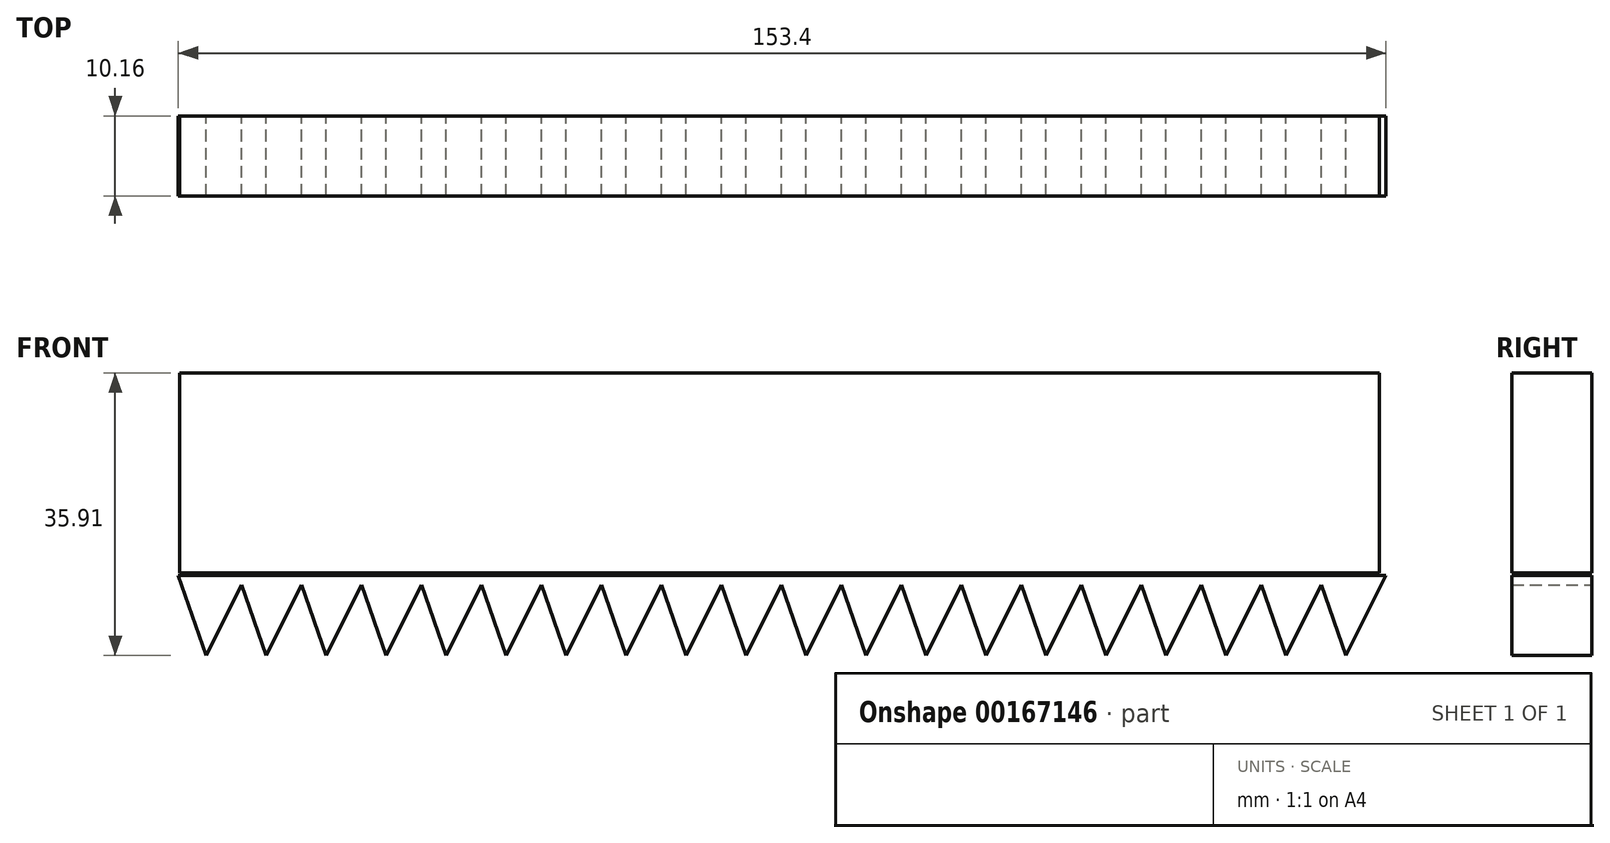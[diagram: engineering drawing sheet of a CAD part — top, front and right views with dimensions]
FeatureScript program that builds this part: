
annotation { "Feature Type Name" : "Feature", "Feature Type Description" : "" }
export const myFeature = defineFeature(function(context is Context, id is Id, definition is map)
    precondition{}
    {
        {
            var Q0;
            Q0=qCreatedBy(makeId("Front.planeOp"),FACE);
            var sketch = newSketch(context, id + "F0", { "sketchPlane" : qUnion([Q0])});
            skLineSegment(sketch, "E0.bottom", {"start": v(-76.2, 12.7) * mm, "end": v(76.2, 12.7) * mm});
            skLineSegment(sketch, "E0.top", {"start": v(-76.2, -12.7) * mm, "end": v(76.2, -12.7) * mm});
            skLineSegment(sketch, "E0.left", {"start": v(-76.2, 12.7) * mm, "end": v(-76.2, -12.7) * mm});
            skLineSegment(sketch, "E0.right", {"start": v(76.2, 12.7) * mm, "end": v(76.2, -12.7) * mm});
            skPoint(sketch, "E0.middle", {"position": v(0, 0) * mm});
            skSolve(sketch);
        }
        {
            var Q0;
            Q0=qCreatedBy(makeId("Front.planeOp"),FACE);
            var sketch = newSketch(context, id + "F1", { "sketchPlane" : qUnion([Q0])});
            skLineSegment(sketch, "E1", {"start": v(-76.4, -13.02) * mm, "end": v(-67.77, -13.02) * mm});
            skLineSegment(sketch, "E2", {"start": v(-76.4, -13.02) * mm, "end": v(-72.87, -23.2) * mm});
            skLineSegment(sketch, "E3", {"start": v(-67.77, -13.02) * mm, "end": v(-72.87, -23.2) * mm});
            skLineSegment(sketch, "E4.1.0.0", {"start": v(-68.77, -13.02) * mm, "end": v(-65.25, -23.2) * mm});
            skLineSegment(sketch, "E4.1.0.1", {"start": v(-60.15, -13.02) * mm, "end": v(-65.25, -23.2) * mm});
            skLineSegment(sketch, "E4.1.0.2", {"start": v(-68.77, -13.02) * mm, "end": v(-60.15, -13.02) * mm});
            skLineSegment(sketch, "E4.2.0.0", {"start": v(-61.15, -13.02) * mm, "end": v(-57.63, -23.2) * mm});
            skLineSegment(sketch, "E4.2.0.1", {"start": v(-52.53, -13.02) * mm, "end": v(-57.63, -23.2) * mm});
            skLineSegment(sketch, "E4.2.0.2", {"start": v(-61.15, -13.02) * mm, "end": v(-52.53, -13.02) * mm});
            skLineSegment(sketch, "E4.3.0.0", {"start": v(-53.53, -13.02) * mm, "end": v(-50, -23.2) * mm});
            skLineSegment(sketch, "E4.3.0.1", {"start": v(-44.91, -13.02) * mm, "end": v(-50, -23.2) * mm});
            skLineSegment(sketch, "E4.3.0.2", {"start": v(-53.53, -13.02) * mm, "end": v(-44.91, -13.02) * mm});
            skLineSegment(sketch, "E4.4.0.0", {"start": v(-45.91, -13.02) * mm, "end": v(-42.39, -23.2) * mm});
            skLineSegment(sketch, "E4.4.0.1", {"start": v(-37.3, -13.02) * mm, "end": v(-42.39, -23.2) * mm});
            skLineSegment(sketch, "E4.4.0.2", {"start": v(-45.91, -13.02) * mm, "end": v(-37.3, -13.02) * mm});
            skLineSegment(sketch, "E4.5.0.0", {"start": v(-38.3, -13.02) * mm, "end": v(-34.77, -23.2) * mm});
            skLineSegment(sketch, "E4.5.0.1", {"start": v(-29.67, -13.02) * mm, "end": v(-34.77, -23.2) * mm});
            skLineSegment(sketch, "E4.5.0.2", {"start": v(-38.3, -13.02) * mm, "end": v(-29.67, -13.02) * mm});
            skLineSegment(sketch, "E4.6.0.0", {"start": v(-30.67, -13.02) * mm, "end": v(-27.15, -23.2) * mm});
            skLineSegment(sketch, "E4.6.0.1", {"start": v(-22.05, -13.02) * mm, "end": v(-27.15, -23.2) * mm});
            skLineSegment(sketch, "E4.6.0.2", {"start": v(-30.67, -13.02) * mm, "end": v(-22.05, -13.02) * mm});
            skLineSegment(sketch, "E4.7.0.0", {"start": v(-23.05, -13.02) * mm, "end": v(-19.53, -23.2) * mm});
            skLineSegment(sketch, "E4.7.0.1", {"start": v(-14.43, -13.02) * mm, "end": v(-19.53, -23.2) * mm});
            skLineSegment(sketch, "E4.7.0.2", {"start": v(-23.05, -13.02) * mm, "end": v(-14.43, -13.02) * mm});
            skLineSegment(sketch, "E4.8.0.0", {"start": v(-15.43, -13.02) * mm, "end": v(-11.9, -23.2) * mm});
            skLineSegment(sketch, "E4.8.0.1", {"start": v(-6.81, -13.02) * mm, "end": v(-11.9, -23.2) * mm});
            skLineSegment(sketch, "E4.8.0.2", {"start": v(-15.43, -13.02) * mm, "end": v(-6.81, -13.02) * mm});
            skLineSegment(sketch, "E4.9.0.0", {"start": v(-7.81, -13.02) * mm, "end": v(-4.29, -23.2) * mm});
            skLineSegment(sketch, "E4.9.0.1", {"start": v(0.8, -13.02) * mm, "end": v(-4.29, -23.2) * mm});
            skLineSegment(sketch, "E4.9.0.2", {"start": v(-7.81, -13.02) * mm, "end": v(0.8, -13.02) * mm});
            skLineSegment(sketch, "E4.10.0.0", {"start": v(-0.2, -13.02) * mm, "end": v(3.33, -23.2) * mm});
            skLineSegment(sketch, "E4.10.0.1", {"start": v(8.43, -13.02) * mm, "end": v(3.33, -23.2) * mm});
            skLineSegment(sketch, "E4.10.0.2", {"start": v(-0.2, -13.02) * mm, "end": v(8.43, -13.02) * mm});
            skLineSegment(sketch, "E4.11.0.0", {"start": v(7.43, -13.02) * mm, "end": v(10.95, -23.2) * mm});
            skLineSegment(sketch, "E4.11.0.1", {"start": v(16.05, -13.02) * mm, "end": v(10.95, -23.2) * mm});
            skLineSegment(sketch, "E4.11.0.2", {"start": v(7.43, -13.02) * mm, "end": v(16.05, -13.02) * mm});
            skLineSegment(sketch, "E4.12.0.0", {"start": v(15.05, -13.02) * mm, "end": v(18.57, -23.2) * mm});
            skLineSegment(sketch, "E4.12.0.1", {"start": v(23.67, -13.02) * mm, "end": v(18.57, -23.2) * mm});
            skLineSegment(sketch, "E4.12.0.2", {"start": v(15.05, -13.02) * mm, "end": v(23.67, -13.02) * mm});
            skLineSegment(sketch, "E4.13.0.0", {"start": v(22.67, -13.02) * mm, "end": v(26.2, -23.2) * mm});
            skLineSegment(sketch, "E4.13.0.1", {"start": v(31.29, -13.02) * mm, "end": v(26.2, -23.2) * mm});
            skLineSegment(sketch, "E4.13.0.2", {"start": v(22.67, -13.02) * mm, "end": v(31.29, -13.02) * mm});
            skLineSegment(sketch, "E4.14.0.0", {"start": v(30.29, -13.02) * mm, "end": v(33.81, -23.2) * mm});
            skLineSegment(sketch, "E4.14.0.1", {"start": v(38.9, -13.02) * mm, "end": v(33.81, -23.2) * mm});
            skLineSegment(sketch, "E4.14.0.2", {"start": v(30.29, -13.02) * mm, "end": v(38.9, -13.02) * mm});
            skLineSegment(sketch, "E4.15.0.0", {"start": v(37.9, -13.02) * mm, "end": v(41.43, -23.2) * mm});
            skLineSegment(sketch, "E4.15.0.1", {"start": v(46.53, -13.02) * mm, "end": v(41.43, -23.2) * mm});
            skLineSegment(sketch, "E4.15.0.2", {"start": v(37.9, -13.02) * mm, "end": v(46.53, -13.02) * mm});
            skLineSegment(sketch, "E4.16.0.0", {"start": v(45.53, -13.02) * mm, "end": v(49.05, -23.2) * mm});
            skLineSegment(sketch, "E4.16.0.1", {"start": v(54.15, -13.02) * mm, "end": v(49.05, -23.2) * mm});
            skLineSegment(sketch, "E4.16.0.2", {"start": v(45.53, -13.02) * mm, "end": v(54.15, -13.02) * mm});
            skLineSegment(sketch, "E4.17.0.0", {"start": v(53.15, -13.02) * mm, "end": v(56.67, -23.2) * mm});
            skLineSegment(sketch, "E4.17.0.1", {"start": v(61.77, -13.02) * mm, "end": v(56.67, -23.2) * mm});
            skLineSegment(sketch, "E4.17.0.2", {"start": v(53.15, -13.02) * mm, "end": v(61.77, -13.02) * mm});
            skLineSegment(sketch, "E4.18.0.0", {"start": v(60.77, -13.02) * mm, "end": v(64.3, -23.2) * mm});
            skLineSegment(sketch, "E4.18.0.1", {"start": v(69.39, -13.02) * mm, "end": v(64.3, -23.2) * mm});
            skLineSegment(sketch, "E4.18.0.2", {"start": v(60.77, -13.02) * mm, "end": v(69.39, -13.02) * mm});
            skLineSegment(sketch, "E4.19.0.0", {"start": v(68.39, -13.02) * mm, "end": v(71.91, -23.2) * mm});
            skLineSegment(sketch, "E4.19.0.1", {"start": v(77, -13.02) * mm, "end": v(71.91, -23.2) * mm});
            skLineSegment(sketch, "E4.19.0.2", {"start": v(68.39, -13.02) * mm, "end": v(77, -13.02) * mm});
            skLineSegment(sketch, "E4.direction1", {"start": v(-72.87, -23.2) * mm, "end": v(-65.25, -23.2) * mm, "construction": true});
            skSolve(sketch);
        }
        {
            var Q0;
            Q0 = qSketchRegion(id + "F0", true);
            var Q1;
            Q1 = qSketchRegion(id + "F1", true);
            extrude(context, id + "F2", {"entities" : qUnion([Q0, Q1]), "depth" : 10.16 * mm});
        }
    });
